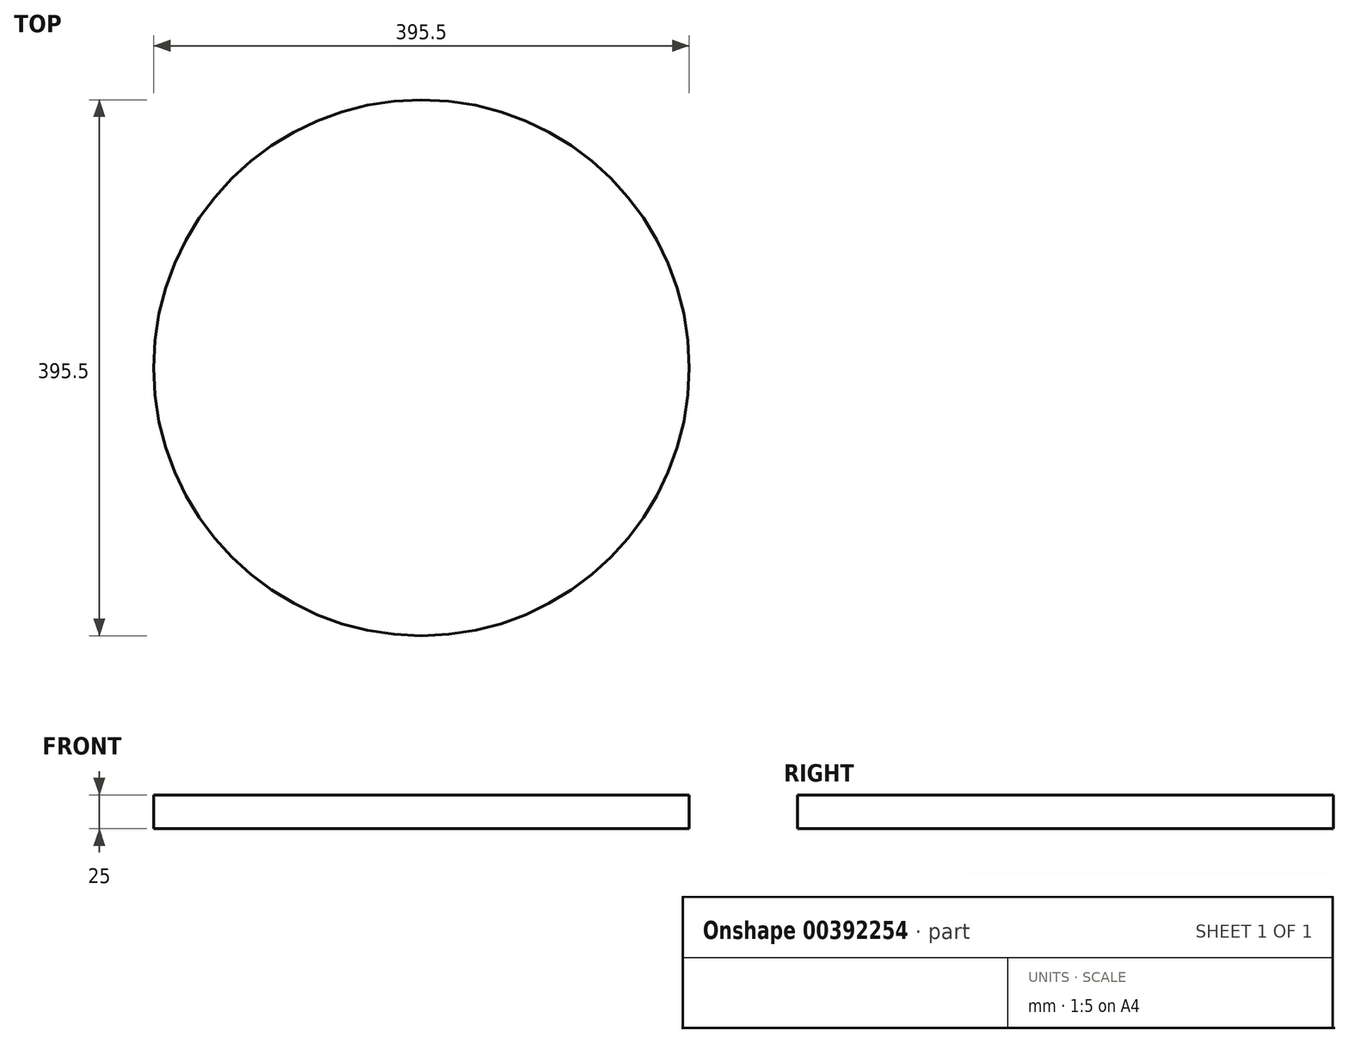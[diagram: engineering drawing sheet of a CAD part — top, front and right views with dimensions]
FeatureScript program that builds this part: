
annotation { "Feature Type Name" : "Feature", "Feature Type Description" : "" }
export const myFeature = defineFeature(function(context is Context, id is Id, definition is map)
    precondition{}
    {
        {
            var Q0;
            Q0=qCreatedBy(makeId("Top.planeOp"),FACE);
            var sketch = newSketch(context, id + "F0", { "sketchPlane" : qUnion([Q0])});
            skCircle(sketch, "E0", {"center": v(0, 0) * mm, "radius": 197.75 * mm});
            skSolve(sketch);
        }
        {
            var Q0;
            Q0 = qSketchRegion(id + "F0", true);
            extrude(context, id + "F1", {"entities" : qUnion([Q0]), "oppositeDirection" : true, "depth" : 25 * mm, "offsetDistance" : 25 * mm});
        }
    });
